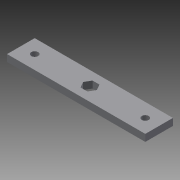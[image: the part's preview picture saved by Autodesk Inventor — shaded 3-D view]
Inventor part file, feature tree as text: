
AUTODESK INVENTOR PART (.ipt)
format: ipt  version: 2013 (Build 170138000, 138)  size: 93,696 bytes
history: native  units: in
note: dims shown in document units (in); Inventor stores cm internally (conversion verified against a paired STEP export)
features: extrude x3, sketch x3
ambient origin geometry x8: Origin, YZ Plane, XZ Plane, XY Plane, X Axis, Y Axis, Z Axis, Center Point
bodies: Solid1 (feature_tree)
feature tree (6):
  extrude  "Extrusion1"  Depth=1.0in
  extrude  "Extrusion2"  Depth=0.5in
  extrude  "Extrusion3"  Depth=0.5in
  sketch  "Sketch1"  dims[d0=5.0in d1=1.0in]
  sketch  "Sketch2"  dims[d2=0.25in d3=0.0in d4=0.5in]
  sketch  "Sketch3"  dims[d5=0.0in d6=0.5in d7=180.0deg d8=0.25in d9=0.25in d10=0.25in d11=0.0in d12=0.5in d13=1.0in d14=0.0in]
